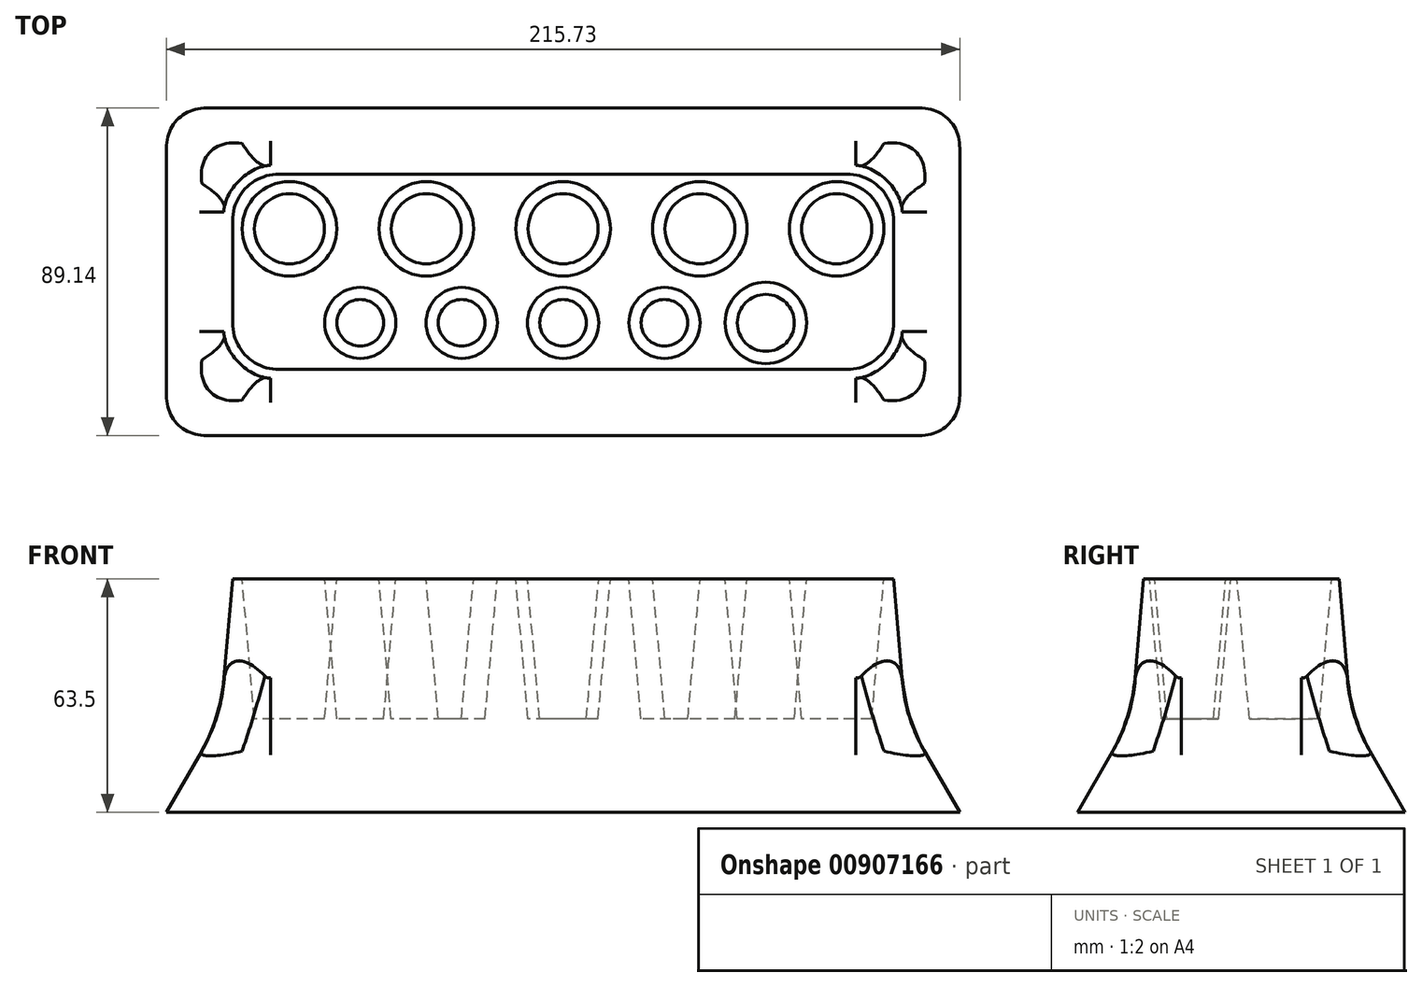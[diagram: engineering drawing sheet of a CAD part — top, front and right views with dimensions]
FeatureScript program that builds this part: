
annotation { "Feature Type Name" : "Feature", "Feature Type Description" : "" }
export const myFeature = defineFeature(function(context is Context, id is Id, definition is map)
    precondition{}
    {
        {
            var Q0;
            Q0=qCreatedBy(makeId("Top.planeOp"),FACE);
            var sketch = newSketch(context, id + "F0", { "sketchPlane" : qUnion([Q0])});
            skLineSegment(sketch, "E0.bottom", {"start": v(0, 0) * mm, "end": v(186.41, 0) * mm});
            skLineSegment(sketch, "E0.top", {"start": v(0, 59.81) * mm, "end": v(186.41, 59.81) * mm});
            skLineSegment(sketch, "E0.left", {"start": v(0, 0) * mm, "end": v(0, 59.81) * mm});
            skLineSegment(sketch, "E0.right", {"start": v(186.41, 0) * mm, "end": v(186.41, 59.81) * mm});
            skCircle(sketch, "E1", {"center": v(18.8, 41.6) * mm, "radius": 9.53 * mm});
            skCircle(sketch, "E2", {"center": v(56, 41.6) * mm, "radius": 9.53 * mm});
            skCircle(sketch, "E3", {"center": v(93.2, 41.6) * mm, "radius": 9.53 * mm});
            skCircle(sketch, "E4", {"center": v(130.4, 41.6) * mm, "radius": 9.53 * mm});
            skCircle(sketch, "E5", {"center": v(167.6, 41.6) * mm, "radius": 9.53 * mm});
            skCircle(sketch, "E6", {"center": v(38.08, 16) * mm, "radius": 6.35 * mm});
            skCircle(sketch, "E7", {"center": v(65.64, 16) * mm, "radius": 6.35 * mm});
            skCircle(sketch, "E8", {"center": v(93.2, 16) * mm, "radius": 6.35 * mm});
            skCircle(sketch, "E9", {"center": v(120.77, 16) * mm, "radius": 6.35 * mm});
            skCircle(sketch, "E10", {"center": v(148.33, 16) * mm, "radius": 7.75 * mm});
            skLineSegment(sketch, "E11", {"start": v(18.8, 41.6) * mm, "end": v(56, 41.6) * mm, "construction": true});
            skLineSegment(sketch, "E12", {"start": v(93.2, 41.6) * mm, "end": v(130.4, 41.6) * mm, "construction": true});
            skLineSegment(sketch, "E13", {"start": v(167.6, 41.6) * mm, "end": v(130.4, 41.6) * mm, "construction": true});
            skLineSegment(sketch, "E14", {"start": v(93.2, 41.6) * mm, "end": v(56, 41.6) * mm, "construction": true});
            skLineSegment(sketch, "E15", {"start": v(38.08, 16) * mm, "end": v(65.64, 16) * mm, "construction": true});
            skLineSegment(sketch, "E16", {"start": v(65.64, 16) * mm, "end": v(93.2, 16) * mm, "construction": true});
            skLineSegment(sketch, "E17", {"start": v(93.2, 16) * mm, "end": v(120.77, 16) * mm, "construction": true});
            skLineSegment(sketch, "E18", {"start": v(120.77, 16) * mm, "end": v(148.33, 16) * mm, "construction": true});
            skLineSegment(sketch, "E19", {"start": v(93.2, 41.6) * mm, "end": v(93.2, 16) * mm, "construction": true});
            skLineSegment(sketch, "E20", {"start": v(93.2, 0) * mm, "end": v(93.2, 16) * mm, "construction": true});
            skSolve(sketch);
        }
        {
            var Q0;
            Q0=makeQuery(id+"F0.imprint","IMPRINT",FACE,{"disambiguationData":[TD([[makeQuery(id+"F0.imprint","IMPRINT",EDGE,{"derivedFrom":sQuery(id+"F0.wireOp",EDGE,"E5")}),1.0]])]});
            var Q1;
            Q1=makeQuery(id+"F0.imprint","IMPRINT",FACE,{"disambiguationData":[TD([[makeQuery(id+"F0.imprint","IMPRINT",EDGE,{"derivedFrom":sQuery(id+"F0.wireOp",EDGE,"E0.bottom")}),1.0]])]});
            var Q2;
            Q2=makeQuery(id+"F0.imprint","IMPRINT",FACE,{"disambiguationData":[TD([[makeQuery(id+"F0.imprint","IMPRINT",EDGE,{"derivedFrom":sQuery(id+"F0.wireOp",EDGE,"E4")}),1.0]])]});
            var Q3;
            Q3=makeQuery(id+"F0.imprint","IMPRINT",FACE,{"disambiguationData":[TD([[makeQuery(id+"F0.imprint","IMPRINT",EDGE,{"derivedFrom":sQuery(id+"F0.wireOp",EDGE,"E10")}),1.0]])]});
            var Q4;
            Q4=makeQuery(id+"F0.imprint","IMPRINT",FACE,{"disambiguationData":[TD([[makeQuery(id+"F0.imprint","IMPRINT",EDGE,{"derivedFrom":sQuery(id+"F0.wireOp",EDGE,"E9")}),1.0]])]});
            var Q5;
            Q5=makeQuery(id+"F0.imprint","IMPRINT",FACE,{"disambiguationData":[TD([[makeQuery(id+"F0.imprint","IMPRINT",EDGE,{"derivedFrom":sQuery(id+"F0.wireOp",EDGE,"E3")}),1.0]])]});
            var Q6;
            Q6=makeQuery(id+"F0.imprint","IMPRINT",FACE,{"disambiguationData":[TD([[makeQuery(id+"F0.imprint","IMPRINT",EDGE,{"derivedFrom":sQuery(id+"F0.wireOp",EDGE,"E8")}),1.0]])]});
            var Q7;
            Q7=makeQuery(id+"F0.imprint","IMPRINT",FACE,{"disambiguationData":[TD([[makeQuery(id+"F0.imprint","IMPRINT",EDGE,{"derivedFrom":sQuery(id+"F0.wireOp",EDGE,"E2")}),1.0]])]});
            var Q8;
            Q8=makeQuery(id+"F0.imprint","IMPRINT",FACE,{"disambiguationData":[TD([[makeQuery(id+"F0.imprint","IMPRINT",EDGE,{"derivedFrom":sQuery(id+"F0.wireOp",EDGE,"E1")}),1.0]])]});
            var Q9;
            Q9=makeQuery(id+"F0.imprint","IMPRINT",FACE,{"disambiguationData":[TD([[makeQuery(id+"F0.imprint","IMPRINT",EDGE,{"derivedFrom":sQuery(id+"F0.wireOp",EDGE,"E6")}),1.0]])]});
            var Q10;
            Q10=makeQuery(id+"F0.imprint","IMPRINT",FACE,{"disambiguationData":[TD([[makeQuery(id+"F0.imprint","IMPRINT",EDGE,{"derivedFrom":sQuery(id+"F0.wireOp",EDGE,"E7")}),1.0]])]});
            extrude(context, id + "F1", {"entities" : qUnion([Q0, Q1, Q2, Q3, Q4, Q5, Q6, Q7, Q8, Q9, Q10]), "oppositeDirection" : true, "depth" : 25.4 * mm, "offsetDistance" : 25.4 * mm, "hasDraft" : true, "draftAngle" : 30 * degree});
        }
        {
            var Q0;
            Q0=qSketchRegion(id+"F0",true);
            extrude(context, id + "F2", {"entities" : qUnion([Q0]), "operationType" : NewBodyOperationType.ADD, "depth" : 38.1 * mm, "offsetDistance" : 25.4 * mm, "hasDraft" : true, "draftAngle" : 5 * degree, "draftPullDirection" : true});
        }
        {
            var Q0;
            Q0=makeQuery(id+"F1.opExtrude","SWEPT_EDGE",EDGE,{"disambiguationData":[OSD([sQuery(id+"F0.wireOp",EDGE,"E0.bottom"),sQuery(id+"F0.wireOp",EDGE,"E0.right")])]});
            var Q1;
            Q1=makeQuery(id+"F2.opExtrude","SWEPT_EDGE",EDGE,{"disambiguationData":[OSD([sQuery(id+"F0.wireOp",EDGE,"E0.bottom"),sQuery(id+"F0.wireOp",EDGE,"E0.right")])]});
            var Q2;
            Q2=makeQuery(id+"F1.opExtrude","SWEPT_EDGE",EDGE,{"disambiguationData":[OSD([sQuery(id+"F0.wireOp",EDGE,"E0.top"),sQuery(id+"F0.wireOp",EDGE,"E0.right")])]});
            var Q3;
            Q3=makeQuery(id+"F2.opExtrude","SWEPT_EDGE",EDGE,{"disambiguationData":[OSD([sQuery(id+"F0.wireOp",EDGE,"E0.top"),sQuery(id+"F0.wireOp",EDGE,"E0.right")])]});
            var Q4;
            Q4=makeQuery(id+"F2.opExtrude","SWEPT_EDGE",EDGE,{"disambiguationData":[OSD([sQuery(id+"F0.wireOp",EDGE,"E0.bottom"),sQuery(id+"F0.wireOp",EDGE,"E0.left")])]});
            var Q5;
            Q5=makeQuery(id+"F1.opExtrude","SWEPT_EDGE",EDGE,{"disambiguationData":[OSD([sQuery(id+"F0.wireOp",EDGE,"E0.bottom"),sQuery(id+"F0.wireOp",EDGE,"E0.left")])]});
            var Q6;
            Q6=makeQuery(id+"F1.opExtrude","SWEPT_EDGE",EDGE,{"disambiguationData":[OSD([sQuery(id+"F0.wireOp",EDGE,"E0.top"),sQuery(id+"F0.wireOp",EDGE,"E0.left")])]});
            var Q7;
            Q7=makeQuery(id+"F2.opExtrude","SWEPT_EDGE",EDGE,{"disambiguationData":[OSD([sQuery(id+"F0.wireOp",EDGE,"E0.top"),sQuery(id+"F0.wireOp",EDGE,"E0.left")])]});
            fillet(context, id + "F3", {"entities" : qUnion([Q0, Q1, Q2, Q3, Q4, Q5, Q6, Q7]), "radius" : 12.7 * mm, "tangentPropagation" : true, "allowEdgeOverflow" : false});
        }
        {
            var Q0;
            {var subQ0=sQuery(id+"F0.wireOp",EDGE,"E0.bottom");Q0=makeQuery(id+"F2.boolean.opBoolean","MERGE",EDGE,{"derivedFrom":[makeQuery(id+"F1.opExtrude","CAP_EDGE",EDGE,{"disambiguationData":[OSD([subQ0])],"isStart":true}),makeQuery(id+"F2.opExtrude","CAP_EDGE",EDGE,{"disambiguationData":[OSD([subQ0])],"isStart":true})]});}
            var Q1;
            {var subQ0=sQuery(id+"F0.wireOp",EDGE,"E0.left");var subQ1=sQuery(id+"F0.wireOp",EDGE,"E0.bottom");Q1=makeQuery(id+"F3.opFillet","BLEND_EDGE",EDGE,{"blendedFrom":[makeQuery(id+"F1.opExtrude","SWEPT_EDGE",EDGE,{"disambiguationData":[OSD([subQ1,subQ0])]}),makeQuery(id+"F2.opExtrude","SWEPT_EDGE",EDGE,{"disambiguationData":[OSD([subQ1,subQ0])]})],"blendedInto":[]});}
            var Q2;
            {var subQ0=sQuery(id+"F0.wireOp",EDGE,"E0.left");Q2=makeQuery(id+"F2.boolean.opBoolean","MERGE",EDGE,{"derivedFrom":[makeQuery(id+"F1.opExtrude","CAP_EDGE",EDGE,{"disambiguationData":[OSD([subQ0])],"isStart":true}),makeQuery(id+"F2.opExtrude","CAP_EDGE",EDGE,{"disambiguationData":[OSD([subQ0])],"isStart":true})]});}
            var Q3;
            {var subQ0=sQuery(id+"F0.wireOp",EDGE,"E0.left");var subQ1=sQuery(id+"F0.wireOp",EDGE,"E0.top");Q3=makeQuery(id+"F3.opFillet","BLEND_EDGE",EDGE,{"blendedFrom":[makeQuery(id+"F1.opExtrude","SWEPT_EDGE",EDGE,{"disambiguationData":[OSD([subQ1,subQ0])]}),makeQuery(id+"F2.opExtrude","SWEPT_EDGE",EDGE,{"disambiguationData":[OSD([subQ1,subQ0])]})],"blendedInto":[]});}
            fillet(context, id + "F4", {"entities" : qUnion([Q0, Q1, Q2, Q3]), "radius" : 50.8 * mm, "tangentPropagation" : true, "allowEdgeOverflow" : false});
        }
    });
